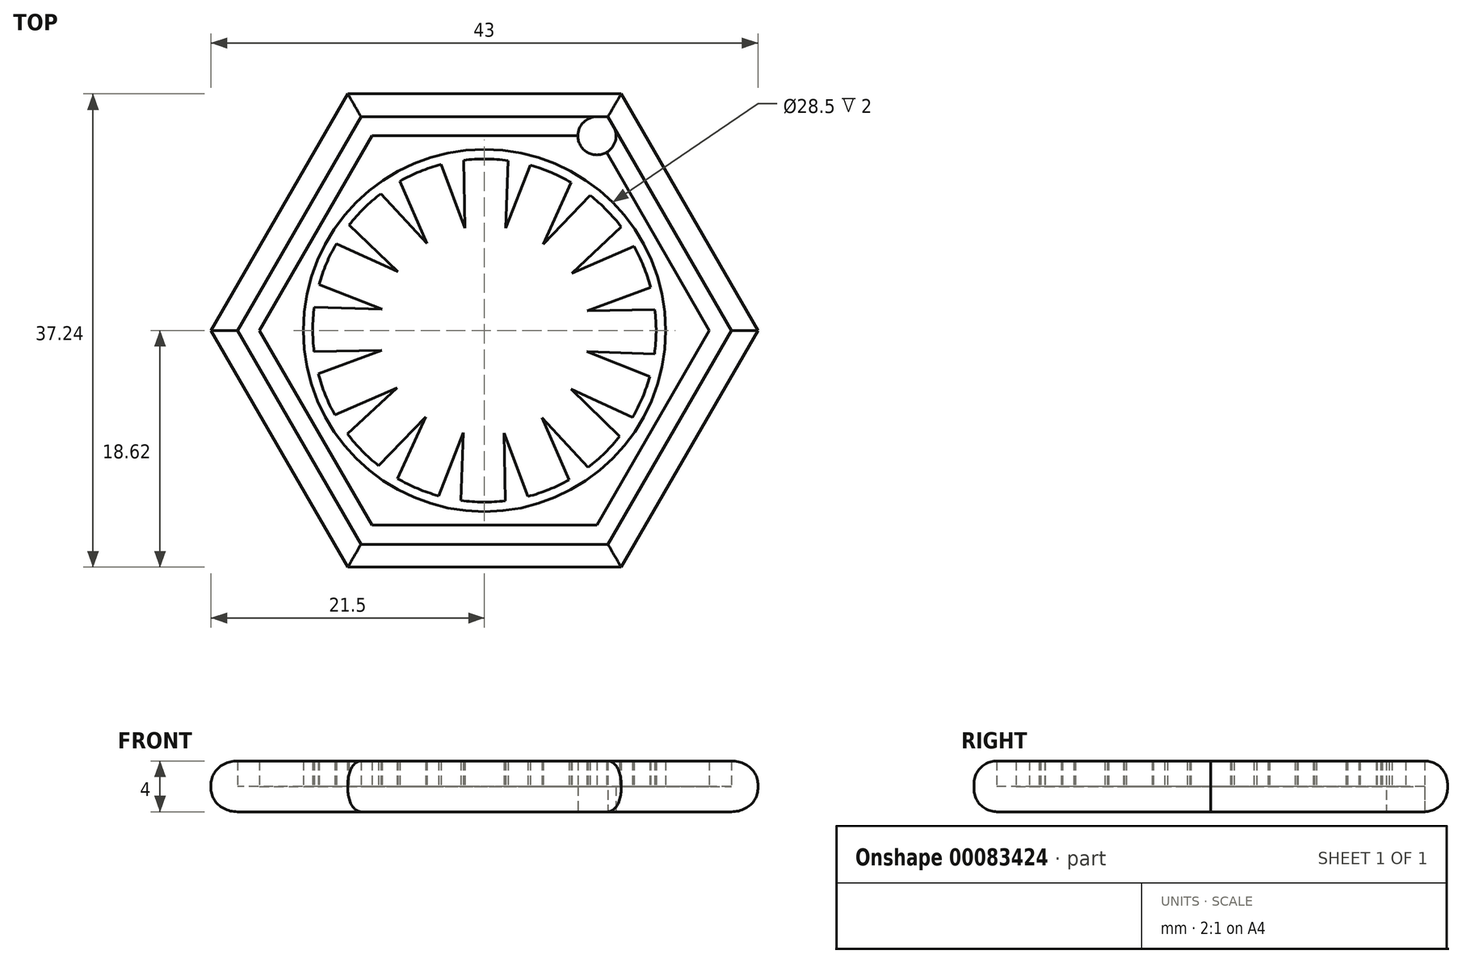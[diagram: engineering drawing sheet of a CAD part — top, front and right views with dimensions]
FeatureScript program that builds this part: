
annotation { "Feature Type Name" : "Feature", "Feature Type Description" : "" }
export const myFeature = defineFeature(function(context is Context, id is Id, definition is map)
    precondition{}
    {
        {
            var Q0;
            Q0=qCreatedBy(makeId("Top.planeOp"),FACE);
            var sketch = newSketch(context, id + "F0", { "sketchPlane" : qUnion([Q0])});
            skCircle(sketch, "E0.cCircle", {"center": v(0, 0) * mm, "radius": 21.5 * mm, "construction": true});
            skLineSegment(sketch, "E0.0", {"start": v(21.5, 0) * mm, "end": v(10.75, -18.62) * mm});
            skLineSegment(sketch, "E0.1", {"start": v(10.75, -18.62) * mm, "end": v(-10.75, -18.62) * mm});
            skLineSegment(sketch, "E0.2", {"start": v(-10.75, -18.62) * mm, "end": v(-21.5, 0) * mm});
            skLineSegment(sketch, "E0.3", {"start": v(-21.5, 0) * mm, "end": v(-10.75, 18.62) * mm});
            skLineSegment(sketch, "E0.4", {"start": v(-10.75, 18.62) * mm, "end": v(10.75, 18.62) * mm});
            skLineSegment(sketch, "E0.5", {"start": v(10.75, 18.62) * mm, "end": v(21.5, 0) * mm});
            skLineSegment(sketch, "E1.0", {"start": v(-9.71, 16.82) * mm, "end": v(9.71, 16.82) * mm});
            skLineSegment(sketch, "E1.1", {"start": v(19.42, 0) * mm, "end": v(9.71, -16.82) * mm});
            skLineSegment(sketch, "E1.2", {"start": v(9.71, -16.82) * mm, "end": v(-9.71, -16.82) * mm});
            skLineSegment(sketch, "E1.3", {"start": v(9.71, 16.82) * mm, "end": v(19.42, 0) * mm});
            skLineSegment(sketch, "E1.4", {"start": v(-9.71, -16.82) * mm, "end": v(-19.42, 0) * mm});
            skLineSegment(sketch, "E1.5", {"start": v(-19.42, 0) * mm, "end": v(-9.71, 16.82) * mm});
            skLineSegment(sketch, "E2.0", {"start": v(-17.69, 0) * mm, "end": v(-8.84, 15.32) * mm});
            skLineSegment(sketch, "E2.1", {"start": v(8.84, 15.32) * mm, "end": v(17.69, 0) * mm});
            skLineSegment(sketch, "E2.2", {"start": v(17.69, 0) * mm, "end": v(8.84, -15.32) * mm});
            skLineSegment(sketch, "E2.3", {"start": v(-8.84, 15.32) * mm, "end": v(8.84, 15.32) * mm});
            skLineSegment(sketch, "E2.4", {"start": v(8.84, -15.32) * mm, "end": v(-8.84, -15.32) * mm});
            skLineSegment(sketch, "E2.5", {"start": v(-8.84, -15.32) * mm, "end": v(-17.69, 0) * mm});
            skCircle(sketch, "E3", {"center": v(0, 0) * mm, "radius": 14.25 * mm});
            skCircle(sketch, "E4", {"center": v(0, 0) * mm, "radius": 13.5 * mm});
            skPoint(sketch, "E5.middle", {"position": v(0, 13.5) * mm});
            skLineSegment(sketch, "E6", {"start": v(3.61, 13) * mm, "end": v(1.66, 8.05) * mm});
            skLineSegment(sketch, "E7", {"start": v(1.85, 13.37) * mm, "end": v(1.66, 8.05) * mm});
            skLineSegment(sketch, "E8.1.0", {"start": v(-3.4, 13.06) * mm, "end": v(-1.54, 8.07) * mm});
            skLineSegment(sketch, "E8.1.1", {"start": v(-1.64, 13.4) * mm, "end": v(-1.54, 8.07) * mm});
            skLineSegment(sketch, "E8.2.0", {"start": v(-8.15, 10.76) * mm, "end": v(-4.52, 6.87) * mm});
            skLineSegment(sketch, "E8.2.1", {"start": v(-6.64, 11.75) * mm, "end": v(-4.52, 6.87) * mm});
            skLineSegment(sketch, "E8.3.0", {"start": v(-11.65, 6.83) * mm, "end": v(-6.8, 4.62) * mm});
            skLineSegment(sketch, "E8.3.1", {"start": v(-10.64, 8.32) * mm, "end": v(-6.8, 4.62) * mm});
            skLineSegment(sketch, "E8.4.0", {"start": v(-13.37, 1.85) * mm, "end": v(-8.05, 1.66) * mm});
            skLineSegment(sketch, "E8.4.1", {"start": v(-13, 3.61) * mm, "end": v(-8.05, 1.66) * mm});
            skLineSegment(sketch, "E8.5.0", {"start": v(-13.06, -3.4) * mm, "end": v(-8.07, -1.54) * mm});
            skLineSegment(sketch, "E8.5.1", {"start": v(-13.4, -1.64) * mm, "end": v(-8.07, -1.54) * mm});
            skLineSegment(sketch, "E8.6.0", {"start": v(-10.76, -8.15) * mm, "end": v(-6.87, -4.52) * mm});
            skLineSegment(sketch, "E8.6.1", {"start": v(-11.75, -6.64) * mm, "end": v(-6.87, -4.52) * mm});
            skLineSegment(sketch, "E8.7.0", {"start": v(-6.83, -11.65) * mm, "end": v(-4.62, -6.8) * mm});
            skLineSegment(sketch, "E8.7.1", {"start": v(-8.32, -10.64) * mm, "end": v(-4.62, -6.8) * mm});
            skLineSegment(sketch, "E8.8.0", {"start": v(-1.85, -13.37) * mm, "end": v(-1.66, -8.05) * mm});
            skLineSegment(sketch, "E8.8.1", {"start": v(-3.61, -13) * mm, "end": v(-1.66, -8.05) * mm});
            skLineSegment(sketch, "E8.9.0", {"start": v(3.4, -13.06) * mm, "end": v(1.54, -8.07) * mm});
            skLineSegment(sketch, "E8.9.1", {"start": v(1.64, -13.4) * mm, "end": v(1.54, -8.07) * mm});
            skLineSegment(sketch, "E8.10.0", {"start": v(8.15, -10.76) * mm, "end": v(4.52, -6.87) * mm});
            skLineSegment(sketch, "E8.10.1", {"start": v(6.64, -11.75) * mm, "end": v(4.52, -6.87) * mm});
            skLineSegment(sketch, "E8.11.0", {"start": v(11.65, -6.83) * mm, "end": v(6.8, -4.62) * mm});
            skLineSegment(sketch, "E8.11.1", {"start": v(10.64, -8.32) * mm, "end": v(6.8, -4.62) * mm});
            skLineSegment(sketch, "E8.12.0", {"start": v(13.37, -1.85) * mm, "end": v(8.05, -1.66) * mm});
            skLineSegment(sketch, "E8.12.1", {"start": v(13, -3.61) * mm, "end": v(8.05, -1.66) * mm});
            skLineSegment(sketch, "E8.13.0", {"start": v(13.06, 3.4) * mm, "end": v(8.07, 1.54) * mm});
            skLineSegment(sketch, "E8.13.1", {"start": v(13.4, 1.64) * mm, "end": v(8.07, 1.54) * mm});
            skLineSegment(sketch, "E8.14.0", {"start": v(10.76, 8.15) * mm, "end": v(6.87, 4.52) * mm});
            skLineSegment(sketch, "E8.14.1", {"start": v(11.75, 6.64) * mm, "end": v(6.87, 4.52) * mm});
            skLineSegment(sketch, "E8.15.0", {"start": v(6.83, 11.65) * mm, "end": v(4.62, 6.8) * mm});
            skLineSegment(sketch, "E8.15.1", {"start": v(8.32, 10.64) * mm, "end": v(4.62, 6.8) * mm});
            skCircle(sketch, "E9", {"center": v(8.84, 15.32) * mm, "radius": 1.5 * mm});
            skSolve(sketch);
        }
        {
            var Q0;
            {var subQ8=sQuery(id+"F0.wireOp",EDGE,"E6");Q0=makeQuery(id+"F0.imprint","IMPRINT",FACE,{"disambiguationData":[TD([[makeQuery(id+"F0.imprint","IMPRINT",EDGE,{"derivedFrom":subQ8}),1.0]])]});}
            var Q1;
            Q1=makeQuery(id+"F0.imprint","IMPRINT",FACE,{"disambiguationData":[TD([[makeQuery(id+"F0.imprint","IMPRINT",EDGE,{"derivedFrom":sQuery(id+"F0.wireOp",EDGE,"E2.0")}),-1.0]])]});
            var Q2;
            Q2=makeQuery(id+"F0.imprint","IMPRINT",FACE,{"disambiguationData":[TD([[makeQuery(id+"F0.imprint","IMPRINT",EDGE,{"derivedFrom":sQuery(id+"F0.wireOp",EDGE,"E0.0")}),-1.0]])]});
            var Q3;
            Q3=makeQuery(id+"F0.imprint","IMPRINT",FACE,{"disambiguationData":[TD([[makeQuery(id+"F0.imprint","IMPRINT",EDGE,{"derivedFrom":sQuery(id+"F0.wireOp",EDGE,"E3")}),1.0]])]});
            var Q4;
            {var subQ0=sQuery(id+"F0.wireOp",EDGE,"E8.6.0");Q4=makeQuery(id+"F0.imprint","IMPRINT",FACE,{"disambiguationData":[TD([[makeQuery(id+"F0.imprint","IMPRINT",EDGE,{"derivedFrom":subQ0}),1.0]])]});}
            var Q5;
            {var subQ0=sQuery(id+"F0.wireOp",EDGE,"E8.7.0");Q5=makeQuery(id+"F0.imprint","IMPRINT",FACE,{"disambiguationData":[TD([[makeQuery(id+"F0.imprint","IMPRINT",EDGE,{"derivedFrom":subQ0}),1.0]])]});}
            var Q6;
            {var subQ0=sQuery(id+"F0.wireOp",EDGE,"E8.8.0");Q6=makeQuery(id+"F0.imprint","IMPRINT",FACE,{"disambiguationData":[TD([[makeQuery(id+"F0.imprint","IMPRINT",EDGE,{"derivedFrom":subQ0}),1.0]])]});}
            var Q7;
            {var subQ0=sQuery(id+"F0.wireOp",EDGE,"E8.9.0");Q7=makeQuery(id+"F0.imprint","IMPRINT",FACE,{"disambiguationData":[TD([[makeQuery(id+"F0.imprint","IMPRINT",EDGE,{"derivedFrom":subQ0}),1.0]])]});}
            var Q8;
            {var subQ0=sQuery(id+"F0.wireOp",EDGE,"E8.10.0");Q8=makeQuery(id+"F0.imprint","IMPRINT",FACE,{"disambiguationData":[TD([[makeQuery(id+"F0.imprint","IMPRINT",EDGE,{"derivedFrom":subQ0}),1.0]])]});}
            var Q9;
            {var subQ0=sQuery(id+"F0.wireOp",EDGE,"E8.11.0");Q9=makeQuery(id+"F0.imprint","IMPRINT",FACE,{"disambiguationData":[TD([[makeQuery(id+"F0.imprint","IMPRINT",EDGE,{"derivedFrom":subQ0}),1.0]])]});}
            var Q10;
            {var subQ0=sQuery(id+"F0.wireOp",EDGE,"E8.12.0");Q10=makeQuery(id+"F0.imprint","IMPRINT",FACE,{"disambiguationData":[TD([[makeQuery(id+"F0.imprint","IMPRINT",EDGE,{"derivedFrom":subQ0}),1.0]])]});}
            var Q11;
            {var subQ0=sQuery(id+"F0.wireOp",EDGE,"E8.13.0");Q11=makeQuery(id+"F0.imprint","IMPRINT",FACE,{"disambiguationData":[TD([[makeQuery(id+"F0.imprint","IMPRINT",EDGE,{"derivedFrom":subQ0}),1.0]])]});}
            var Q12;
            {var subQ0=sQuery(id+"F0.wireOp",EDGE,"E8.14.0");Q12=makeQuery(id+"F0.imprint","IMPRINT",FACE,{"disambiguationData":[TD([[makeQuery(id+"F0.imprint","IMPRINT",EDGE,{"derivedFrom":subQ0}),1.0]])]});}
            var Q13;
            {var subQ0=sQuery(id+"F0.wireOp",EDGE,"E8.15.0");Q13=makeQuery(id+"F0.imprint","IMPRINT",FACE,{"disambiguationData":[TD([[makeQuery(id+"F0.imprint","IMPRINT",EDGE,{"derivedFrom":subQ0}),1.0]])]});}
            var Q14;
            {var subQ0=sQuery(id+"F0.wireOp",EDGE,"E6");Q14=makeQuery(id+"F0.imprint","IMPRINT",FACE,{"disambiguationData":[TD([[makeQuery(id+"F0.imprint","IMPRINT",EDGE,{"derivedFrom":subQ0}),-1.0]])]});}
            var Q15;
            {var subQ0=sQuery(id+"F0.wireOp",EDGE,"E8.1.0");Q15=makeQuery(id+"F0.imprint","IMPRINT",FACE,{"disambiguationData":[TD([[makeQuery(id+"F0.imprint","IMPRINT",EDGE,{"derivedFrom":subQ0}),1.0]])]});}
            var Q16;
            {var subQ0=sQuery(id+"F0.wireOp",EDGE,"E8.2.0");Q16=makeQuery(id+"F0.imprint","IMPRINT",FACE,{"disambiguationData":[TD([[makeQuery(id+"F0.imprint","IMPRINT",EDGE,{"derivedFrom":subQ0}),1.0]])]});}
            var Q17;
            {var subQ0=sQuery(id+"F0.wireOp",EDGE,"E8.3.0");Q17=makeQuery(id+"F0.imprint","IMPRINT",FACE,{"disambiguationData":[TD([[makeQuery(id+"F0.imprint","IMPRINT",EDGE,{"derivedFrom":subQ0}),1.0]])]});}
            var Q18;
            {var subQ0=sQuery(id+"F0.wireOp",EDGE,"E8.4.0");Q18=makeQuery(id+"F0.imprint","IMPRINT",FACE,{"disambiguationData":[TD([[makeQuery(id+"F0.imprint","IMPRINT",EDGE,{"derivedFrom":subQ0}),1.0]])]});}
            var Q19;
            {var subQ0=sQuery(id+"F0.wireOp",EDGE,"E8.5.0");Q19=makeQuery(id+"F0.imprint","IMPRINT",FACE,{"disambiguationData":[TD([[makeQuery(id+"F0.imprint","IMPRINT",EDGE,{"derivedFrom":subQ0}),1.0]])]});}
            var Q20;
            {var subQ5=sQuery(id+"F0.wireOp",EDGE,"E1.1");Q20=makeQuery(id+"F0.imprint","IMPRINT",FACE,{"disambiguationData":[TD([[makeQuery(id+"F0.imprint","IMPRINT",EDGE,{"derivedFrom":subQ5}),-1.0]])]});}
            extrude(context, id + "F1", {"entities" : qUnion([Q0, Q1, Q2, Q3, Q4, Q5, Q6, Q7, Q8, Q9, Q10, Q11, Q12, Q13, Q14, Q15, Q16, Q17, Q18, Q19, Q20]), "depth" : 2 * mm});
        }
        {
            var Q0;
            {var subQ8=sQuery(id+"F0.wireOp",EDGE,"E6");Q0=makeQuery(id+"F0.imprint","IMPRINT",FACE,{"disambiguationData":[TD([[makeQuery(id+"F0.imprint","IMPRINT",EDGE,{"derivedFrom":subQ8}),1.0]])]});}
            var Q1;
            Q1=makeQuery(id+"F0.imprint","IMPRINT",FACE,{"disambiguationData":[TD([[makeQuery(id+"F0.imprint","IMPRINT",EDGE,{"derivedFrom":sQuery(id+"F0.wireOp",EDGE,"E2.0")}),-1.0]])]});
            var Q2;
            Q2=makeQuery(id+"F0.imprint","IMPRINT",FACE,{"disambiguationData":[TD([[makeQuery(id+"F0.imprint","IMPRINT",EDGE,{"derivedFrom":sQuery(id+"F0.wireOp",EDGE,"E0.0")}),-1.0]])]});
            extrude(context, id + "F2", {"entities" : qUnion([Q0, Q1, Q2]), "operationType" : NewBodyOperationType.ADD, "depth" : 4 * mm});
        }
        {
            var Q0;
            Q0=makeQuery(id+"F2.opExtrude","CAP_EDGE",EDGE,{"disambiguationData":[OSD([sQuery(id+"F0.wireOp",EDGE,"E0.2")])],"isStart":false});
            var Q1;
            Q1=makeQuery(id+"F2.opExtrude","CAP_EDGE",EDGE,{"disambiguationData":[OSD([sQuery(id+"F0.wireOp",EDGE,"E0.3")])],"isStart":false});
            var Q2;
            Q2=makeQuery(id+"F2.opExtrude","CAP_EDGE",EDGE,{"disambiguationData":[OSD([sQuery(id+"F0.wireOp",EDGE,"E0.4")])],"isStart":false});
            var Q3;
            Q3=makeQuery(id+"F2.opExtrude","CAP_EDGE",EDGE,{"disambiguationData":[OSD([sQuery(id+"F0.wireOp",EDGE,"E0.5")])],"isStart":false});
            var Q4;
            Q4=makeQuery(id+"F2.opExtrude","CAP_EDGE",EDGE,{"disambiguationData":[OSD([sQuery(id+"F0.wireOp",EDGE,"E0.0")])],"isStart":false});
            var Q5;
            Q5=makeQuery(id+"F2.opExtrude","CAP_EDGE",EDGE,{"disambiguationData":[OSD([sQuery(id+"F0.wireOp",EDGE,"E0.1")])],"isStart":false});
            var Q6;
            Q6=makeQuery(id+"F1.opExtrude","CAP_EDGE",EDGE,{"disambiguationData":[OSD([sQuery(id+"F0.wireOp",EDGE,"E0.0")])],"isStart":true});
            var Q7;
            Q7=makeQuery(id+"F1.opExtrude","CAP_EDGE",EDGE,{"disambiguationData":[OSD([sQuery(id+"F0.wireOp",EDGE,"E0.1")])],"isStart":true});
            var Q8;
            Q8=makeQuery(id+"F1.opExtrude","CAP_EDGE",EDGE,{"disambiguationData":[OSD([sQuery(id+"F0.wireOp",EDGE,"E0.5")])],"isStart":true});
            var Q9;
            Q9=makeQuery(id+"F1.opExtrude","CAP_EDGE",EDGE,{"disambiguationData":[OSD([sQuery(id+"F0.wireOp",EDGE,"E0.4")])],"isStart":true});
            var Q10;
            Q10=makeQuery(id+"F1.opExtrude","CAP_EDGE",EDGE,{"disambiguationData":[OSD([sQuery(id+"F0.wireOp",EDGE,"E0.3")])],"isStart":true});
            var Q11;
            Q11=makeQuery(id+"F1.opExtrude","CAP_EDGE",EDGE,{"disambiguationData":[OSD([sQuery(id+"F0.wireOp",EDGE,"E0.2")])],"isStart":true});
            fillet(context, id + "F3", {"entities" : qUnion([Q0, Q1, Q2, Q3, Q4, Q5, Q6, Q7, Q8, Q9, Q10, Q11]), "radius" : 1.8 * mm, "tangentPropagation" : true, "allowEdgeOverflow" : false});
        }
    });
